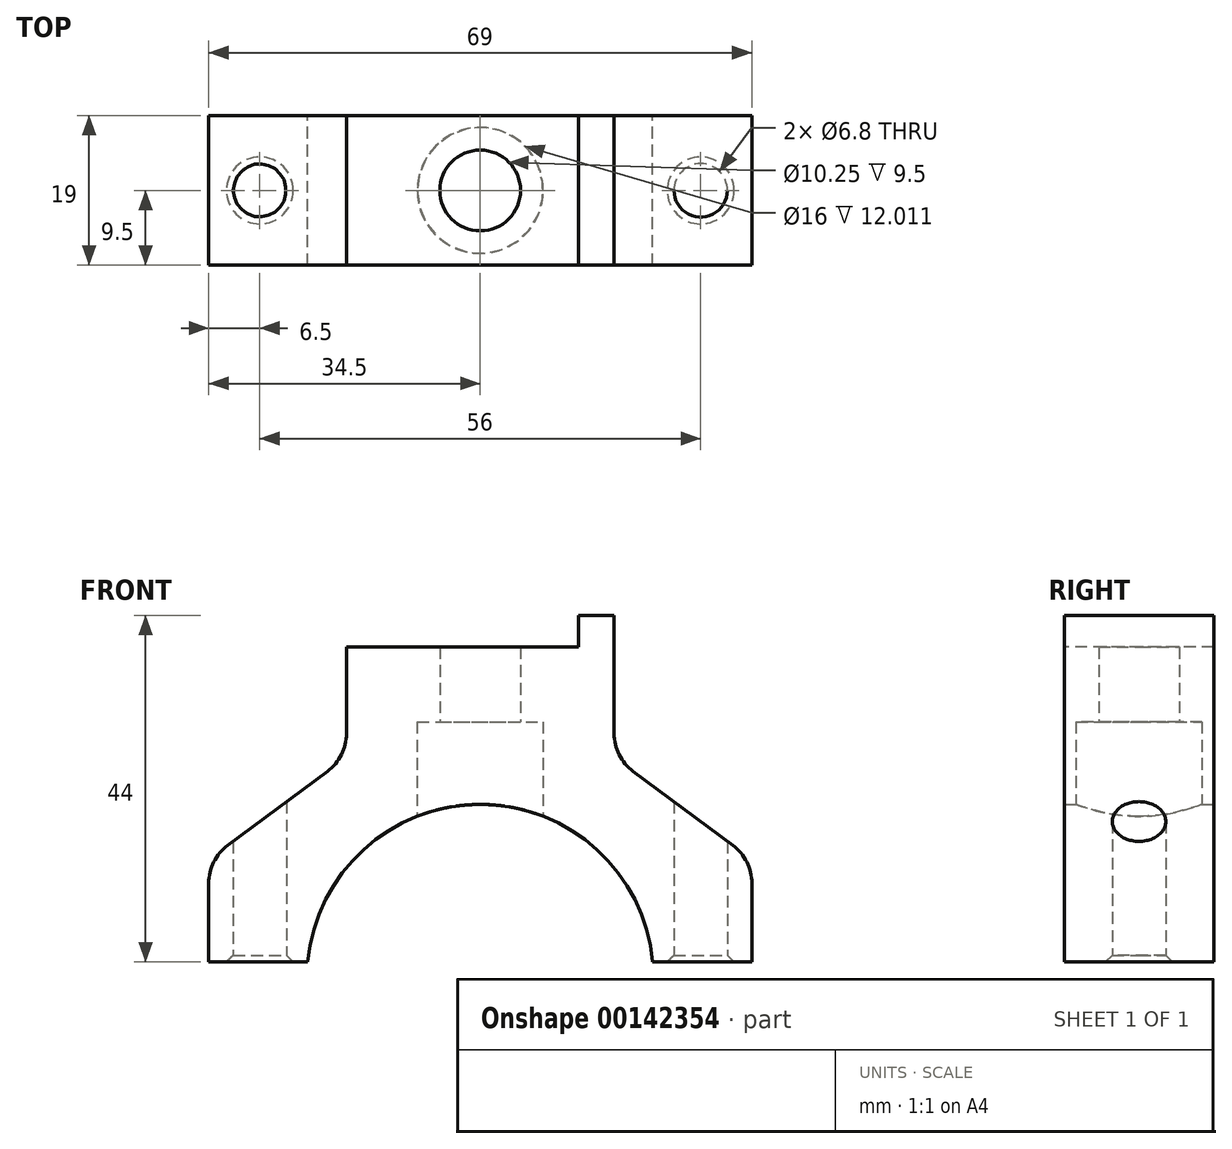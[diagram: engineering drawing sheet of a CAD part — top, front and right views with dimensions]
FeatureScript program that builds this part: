
annotation { "Feature Type Name" : "Feature", "Feature Type Description" : "" }
export const myFeature = defineFeature(function(context is Context, id is Id, definition is map)
    precondition{}
    {
        {
            var Q0;
            Q0=qCreatedBy(makeId("Front.planeOp"),FACE);
            var sketch = newSketch(context, id + "F0", { "sketchPlane" : qUnion([Q0])});
            skArc(sketch, "E0", {"start": v(-21.9, 2) * mm, "mid": v(-14.83, 16.25) * mm, "end": v(0, 22) * mm});
            skLineSegment(sketch, "E1", {"start": v(-34.5, 2) * mm, "end": v(-34.5, 15) * mm});
            skLineSegment(sketch, "E2", {"start": v(-34.5, 15) * mm, "end": v(-17, 28) * mm});
            skLineSegment(sketch, "E3", {"start": v(-17, 28) * mm, "end": v(-17, 46) * mm});
            skLineSegment(sketch, "E4", {"start": v(-17, 46) * mm, "end": v(0, 46) * mm});
            skLineSegment(sketch, "E5", {"start": v(0, 0) * mm, "end": v(0, 46) * mm, "construction": true});
            skPoint(sketch, "E6.orphan", {"position": v(22, 0) * mm});
            skLineSegment(sketch, "E7.MirrorCS", {"start": v(17, 46) * mm, "end": v(0, 46) * mm});
            skLineSegment(sketch, "E8.MirrorCS", {"start": v(17, 28) * mm, "end": v(17, 46) * mm});
            skLineSegment(sketch, "E9.MirrorCS", {"start": v(34.5, 15) * mm, "end": v(17, 28) * mm});
            skLineSegment(sketch, "E10.MirrorCS", {"start": v(34.5, 2) * mm, "end": v(34.5, 15) * mm});
            skArc(sketch, "E11.MirrorCS", {"start": v(21.9, 2) * mm, "mid": v(14.83, 16.25) * mm, "end": v(0, 22) * mm});
            skLineSegment(sketch, "E12", {"start": v(-40.16, 2) * mm, "end": v(42.73, 2) * mm, "construction": true});
            skLineSegment(sketch, "E13", {"start": v(21.9, 2) * mm, "end": v(34.5, 2) * mm});
            skLineSegment(sketch, "E14", {"start": v(-34.5, 2) * mm, "end": v(-21.9, 2) * mm});
            skPoint(sketch, "E15.orphan", {"position": v(34.5, 1) * mm});
            skPoint(sketch, "E16.orphan", {"position": v(-22, 0) * mm});
            skPoint(sketch, "E17.orphan", {"position": v(-34.5, 1) * mm});
            skSolve(sketch);
        }
        {
            var Q0;
            Q0 = qSketchRegion(id + "F0", true);
            extrude(context, id + "F1", {"entities" : qUnion([Q0]), "endBound" : BoundingType.SYMMETRIC, "depth" : 19 * mm});
        }
        {
            var Q0;
            Q0=qCreatedBy(makeId("Top.planeOp"),FACE);
            var sketch = newSketch(context, id + "F2", { "sketchPlane" : qUnion([Q0])});
            skPoint(sketch, "E18", {"position": v(-28, 0) * mm});
            skLineSegment(sketch, "E19", {"start": v(0, 33.05) * mm, "end": v(0, -22.03) * mm, "construction": true});
            skPoint(sketch, "E20.MirrorP", {"position": v(28, 0) * mm});
            skSolve(sketch);
        }
        {
            var Q0;
            Q0=sQuery(id+"F2.wireOp",VERTEX,"E20.MirrorP");
            var Q1;
            Q1=sQuery(id+"F2.wireOp",VERTEX,"E18");
            var Q2;
            Q2=makeQuery(id+"F1.opExtrude","SWEPT_BODY",BODY,{"disambiguationData":[OSD([sQuery(id+"F0.wireOp",EDGE,"E0"),sQuery(id+"F0.wireOp",EDGE,"UEe8GUT3-BfUf-DLK1-vOLE-91k8sVN4rBZw"),sQuery(id+"F0.wireOp",EDGE,"E1"),sQuery(id+"F0.wireOp",EDGE,"E2"),sQuery(id+"F0.wireOp",EDGE,"E3"),sQuery(id+"F0.wireOp",EDGE,"E4"),sQuery(id+"F0.wireOp",EDGE,"E7.MirrorCS"),sQuery(id+"F0.wireOp",EDGE,"E8.MirrorCS"),sQuery(id+"F0.wireOp",EDGE,"E9.MirrorCS"),sQuery(id+"F0.wireOp",EDGE,"E10.MirrorCS"),sQuery(id+"F0.wireOp",EDGE,"87c8850a-f8bb-414c-903e-ebd6c874736d4.MirrorCS"),sQuery(id+"F0.wireOp",EDGE,"E11.MirrorCS")])]});
            hole(context, id + "F3", {"style" : HoleStyle.C_SINK, "endStyle" : HoleEndStyle.THROUGH, "oppositeDirection" : true, "holeDiameter" : 6.8 * mm, "cSinkDiameter" : 8.5 * mm, "cSinkAngle" : 90 * degree, "locations" : qUnion([Q0, Q1]), "scope" : qUnion([Q2]), "tappedDepth" : 12 * mm, "tapClearance" : 3});
        }
        {
            var Q0;
            Q0=qCreatedBy(makeId("Top.planeOp"),FACE);
            var sketch = newSketch(context, id + "F4", { "sketchPlane" : qUnion([Q0])});
            skPoint(sketch, "E21", {"position": v(0, 0) * mm});
            skSolve(sketch);
        }
        {
            var Q0;
            Q0=sQuery(id+"F4.wireOp",VERTEX,"E21");
            var Q1;
            Q1=makeQuery(id+"F1.opExtrude","SWEPT_BODY",BODY,{"disambiguationData":[OSD([sQuery(id+"F0.wireOp",EDGE,"E0"),sQuery(id+"F0.wireOp",EDGE,"UEe8GUT3-BfUf-DLK1-vOLE-91k8sVN4rBZw"),sQuery(id+"F0.wireOp",EDGE,"E1"),sQuery(id+"F0.wireOp",EDGE,"E2"),sQuery(id+"F0.wireOp",EDGE,"E3"),sQuery(id+"F0.wireOp",EDGE,"E4"),sQuery(id+"F0.wireOp",EDGE,"E7.MirrorCS"),sQuery(id+"F0.wireOp",EDGE,"E8.MirrorCS"),sQuery(id+"F0.wireOp",EDGE,"E9.MirrorCS"),sQuery(id+"F0.wireOp",EDGE,"E10.MirrorCS"),sQuery(id+"F0.wireOp",EDGE,"87c8850a-f8bb-414c-903e-ebd6c874736d4.MirrorCS"),sQuery(id+"F0.wireOp",EDGE,"E11.MirrorCS")])]});
            hole(context, id + "F5", {"style" : HoleStyle.C_BORE, "endStyle" : HoleEndStyle.THROUGH, "oppositeDirection" : true, "holeDiameter" : 10.25 * mm, "cBoreDiameter" : 16 * mm, "cBoreDepth" : 10.5 * mm, "locations" : qUnion([Q0]), "scope" : qUnion([Q1]), "tappedDepth" : 12 * mm, "tapClearance" : 3});
        }
        {
            var Q0;
            Q0=makeQuery(id+"F1.opExtrude","CAP_FACE",FACE,{"disambiguationData":[OSD([sQuery(id+"F0.wireOp",EDGE,"E0"),sQuery(id+"F0.wireOp",EDGE,"UEe8GUT3-BfUf-DLK1-vOLE-91k8sVN4rBZw"),sQuery(id+"F0.wireOp",EDGE,"E1"),sQuery(id+"F0.wireOp",EDGE,"E2"),sQuery(id+"F0.wireOp",EDGE,"E3"),sQuery(id+"F0.wireOp",EDGE,"E4"),sQuery(id+"F0.wireOp",EDGE,"E7.MirrorCS"),sQuery(id+"F0.wireOp",EDGE,"E8.MirrorCS"),sQuery(id+"F0.wireOp",EDGE,"E9.MirrorCS"),sQuery(id+"F0.wireOp",EDGE,"E10.MirrorCS"),sQuery(id+"F0.wireOp",EDGE,"87c8850a-f8bb-414c-903e-ebd6c874736d4.MirrorCS"),sQuery(id+"F0.wireOp",EDGE,"E11.MirrorCS")])],"isStart":false});
            var sketch = newSketch(context, id + "F6", { "sketchPlane" : qUnion([Q0])});
            skLineSegment(sketch, "E22.bottom", {"start": v(-17, 46) * mm, "end": v(12.5, 46) * mm});
            skLineSegment(sketch, "E22.top", {"start": v(-17, 42) * mm, "end": v(12.5, 42) * mm});
            skLineSegment(sketch, "E22.left", {"start": v(-17, 46) * mm, "end": v(-17, 42) * mm});
            skLineSegment(sketch, "E22.right", {"start": v(12.5, 46) * mm, "end": v(12.5, 42) * mm});
            skSolve(sketch);
        }
        {
            var Q0;
            Q0 = qSketchRegion(id + "F6", true);
            extrude(context, id + "F7", {"entities" : qUnion([Q0]), "operationType" : NewBodyOperationType.REMOVE, "oppositeDirection" : true, "depth" : 19 * mm});
        }
        {
            var Q0;
            Q0=makeQuery(id+"F1.opExtrude","SWEPT_EDGE",EDGE,{"disambiguationData":[OSD([sQuery(id+"F0.wireOp",EDGE,"E8.MirrorCS"),sQuery(id+"F0.wireOp",EDGE,"E9.MirrorCS")])]});
            var Q1;
            Q1=makeQuery(id+"F1.opExtrude","SWEPT_EDGE",EDGE,{"disambiguationData":[OSD([sQuery(id+"F0.wireOp",EDGE,"E2"),sQuery(id+"F0.wireOp",EDGE,"E3")])]});
            fillet(context, id + "F8", {"entities" : qUnion([Q0, Q1]), "radius" : 6 * mm, "tangentPropagation" : true, "allowEdgeOverflow" : false});
        }
        {
            var Q0;
            Q0=makeQuery(id+"F1.opExtrude","SWEPT_EDGE",EDGE,{"disambiguationData":[OSD([sQuery(id+"F0.wireOp",EDGE,"E9.MirrorCS"),sQuery(id+"F0.wireOp",EDGE,"E10.MirrorCS")])]});
            var Q1;
            Q1=makeQuery(id+"F1.opExtrude","SWEPT_EDGE",EDGE,{"disambiguationData":[OSD([sQuery(id+"F0.wireOp",EDGE,"E1"),sQuery(id+"F0.wireOp",EDGE,"E2")])]});
            fillet(context, id + "F9", {"entities" : qUnion([Q0, Q1]), "radius" : 6 * mm, "tangentPropagation" : true, "allowEdgeOverflow" : false});
        }
    });
